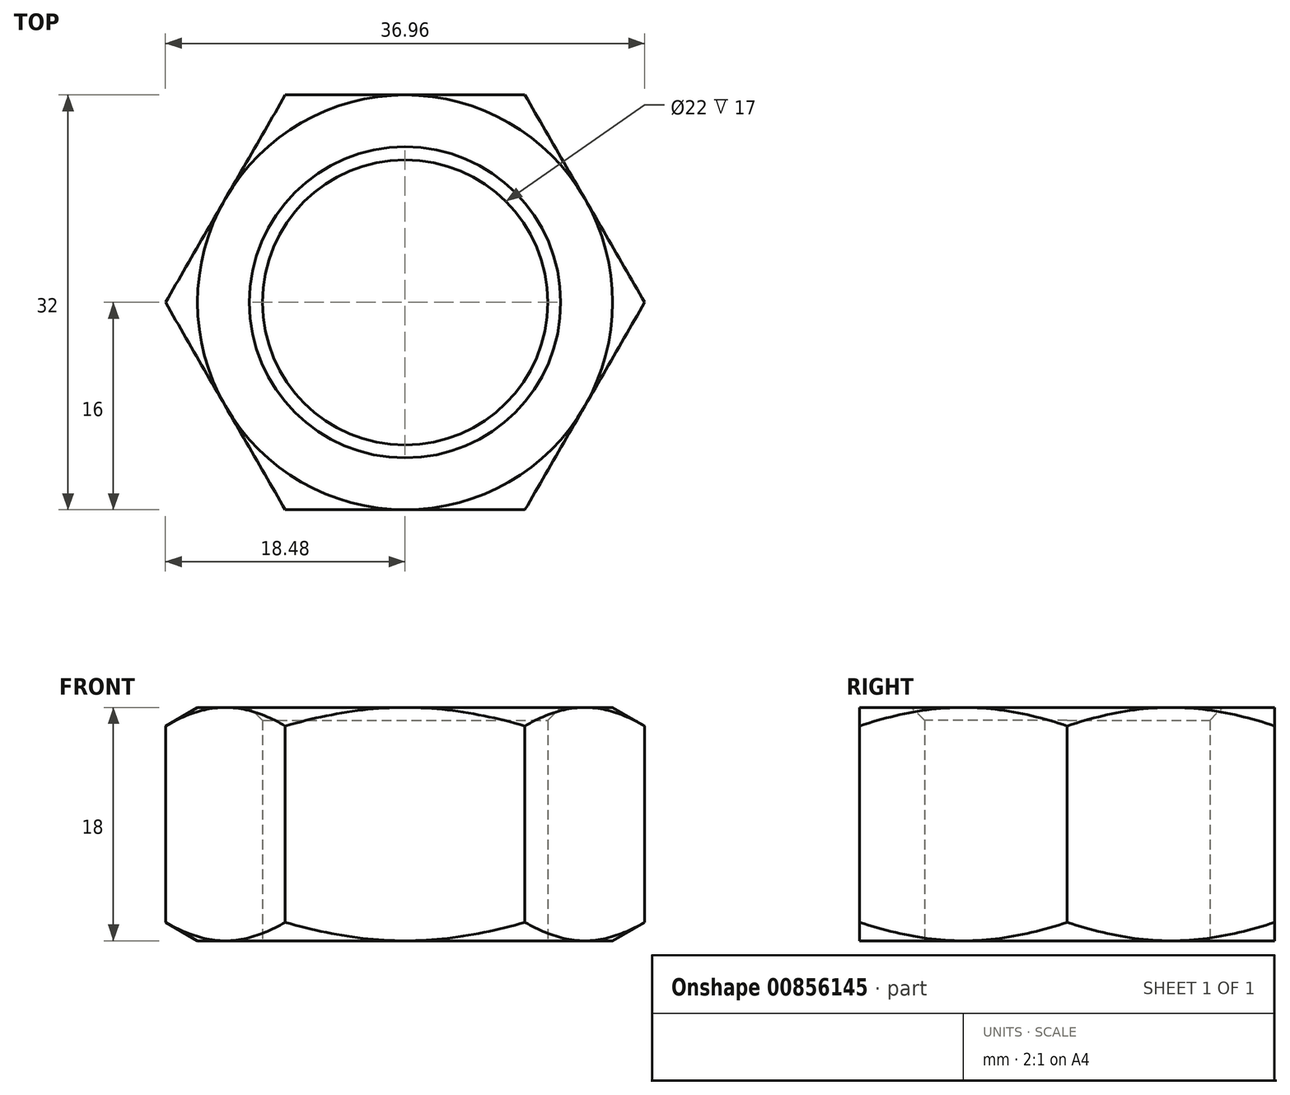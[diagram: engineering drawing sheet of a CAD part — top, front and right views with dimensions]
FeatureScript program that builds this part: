
annotation { "Feature Type Name" : "Feature", "Feature Type Description" : "" }
export const myFeature = defineFeature(function(context is Context, id is Id, definition is map)
    precondition{}
    {
        {
            var Q0;
            Q0=qCreatedBy(makeId("Top.planeOp"),FACE);
            var sketch = newSketch(context, id + "F0", { "sketchPlane" : qUnion([Q0])});
            skCircle(sketch, "E0.cCircle", {"center": v(0, 0) * mm, "radius": 16 * mm, "construction": true});
            skLineSegment(sketch, "E0.0", {"start": v(9.24, 16) * mm, "end": v(18.48, 0) * mm});
            skLineSegment(sketch, "E0.1", {"start": v(18.48, 0) * mm, "end": v(9.24, -16) * mm});
            skLineSegment(sketch, "E0.2", {"start": v(9.24, -16) * mm, "end": v(-9.24, -16) * mm});
            skLineSegment(sketch, "E0.3", {"start": v(-9.24, -16) * mm, "end": v(-18.48, 0) * mm});
            skLineSegment(sketch, "E0.4", {"start": v(-18.48, 0) * mm, "end": v(-9.24, 16) * mm});
            skLineSegment(sketch, "E0.5", {"start": v(-9.24, 16) * mm, "end": v(9.24, 16) * mm});
            skPoint(sketch, "E0.0.midPoint", {"position": v(13.86, 8) * mm});
            skSolve(sketch);
        }
        {
            var Q0;
            Q0=makeQuery(id+"F0.imprint","IMPRINT",FACE,{"disambiguationData":[TD([[makeQuery(id+"F0.imprint","IMPRINT",EDGE,{"derivedFrom":sQuery(id+"F0.wireOp",EDGE,"E0.0")}),-1.0]])]});
            extrude(context, id + "F1", {"entities" : qUnion([Q0]), "depth" : 18 * mm, "offsetDistance" : 25 * mm});
        }
        {
            var Q0;
            Q0=qCreatedBy(makeId("Right.planeOp"),FACE);
            var sketch = newSketch(context, id + "F2", { "sketchPlane" : qUnion([Q0])});
            skLineSegment(sketch, "E1", {"start": v(-16, 18) * mm, "end": v(-29.05, 18) * mm});
            skLineSegment(sketch, "E2", {"start": v(-29.05, 18) * mm, "end": v(-29.05, 10.47) * mm});
            skLineSegment(sketch, "E3", {"start": v(-29.05, 10.47) * mm, "end": v(-16, 18) * mm});
            skLineSegment(sketch, "E4", {"start": v(0, 0) * mm, "end": v(0, 20.15) * mm, "construction": true});
            skLineSegment(sketch, "E5", {"start": v(-16, 9) * mm, "end": v(24.29, 9) * mm, "construction": true});
            skLineSegment(sketch, "E6.MirrorCS", {"start": v(-29.05, 7.53) * mm, "end": v(-16, 0) * mm});
            skLineSegment(sketch, "E7.MirrorCS", {"start": v(-16, 0) * mm, "end": v(-29.05, 0) * mm});
            skLineSegment(sketch, "E8.MirrorCS", {"start": v(-29.05, 0) * mm, "end": v(-29.05, 7.53) * mm});
            skSolve(sketch);
        }
        {
            var Q0;
            Q0=makeQuery(id+"F2.imprint","IMPRINT",FACE,{"disambiguationData":[TD([[makeQuery(id+"F2.imprint","IMPRINT",EDGE,{"derivedFrom":sQuery(id+"F2.wireOp",EDGE,"E1")}),1.0]])]});
            var Q1;
            {var subQ5=sQuery(id+"F2.wireOp",EDGE,"E7.MirrorCS");Q1=makeQuery(id+"F2.imprint","IMPRINT",FACE,{"disambiguationData":[TD([[makeQuery(id+"F2.imprint","IMPRINT",EDGE,{"derivedFrom":subQ5}),-1.0]])]});}
            var Q2;
            {var subQ0=sQuery(id+"F2.wireOp",EDGE,"E8.MirrorCS");var subQ1=sQuery(id+"F2.wireOp",EDGE,"E3");var subQ2=makeQuery(id+"F2.imprint","INTERSECT",VERTEX,{"derivedFrom":[subQ1,subQ0]});Q2=makeQuery(id+"F2.imprint","IMPRINT",FACE,{"disambiguationData":[TD([[makeQuery(id+"F2.imprint","IMPRINT",EDGE,{"disambiguationData":[TD([[subQ2,-1.0]])],"derivedFrom":subQ1}),1.0]])]});}
            var Q3;
            Q3=sQuery(id+"F2.wireOp",EDGE,"E4");
            revolve(context, id + "F3", {"operationType" : NewBodyOperationType.REMOVE, "surfaceOperationType" : NewSurfaceOperationType.NEW, "entities" : qUnion([Q0, Q1, Q2]), "axis" : qUnion([Q3]), "revolveType" : RevolveType.FULL, "oppositeDirection" : true});
        }
        {
            var Q0;
            Q0=makeQuery(id+"F1.opExtrude","CAP_FACE",FACE,{"disambiguationData":[OSD([sQuery(id+"F0.wireOp",EDGE,"E0.0"),sQuery(id+"F0.wireOp",EDGE,"E0.1"),sQuery(id+"F0.wireOp",EDGE,"E0.2"),sQuery(id+"F0.wireOp",EDGE,"E0.3"),sQuery(id+"F0.wireOp",EDGE,"E0.4"),sQuery(id+"F0.wireOp",EDGE,"E0.5")])],"isStart":true});
            var sketch = newSketch(context, id + "F4", { "sketchPlane" : qUnion([Q0])});
            skCircle(sketch, "E9", {"center": v(0, 0) * mm, "radius": 11 * mm});
            skSolve(sketch);
        }
        {
            var Q0;
            Q0=makeQuery(id+"F4.imprint","IMPRINT",FACE,{"disambiguationData":[TD([[makeQuery(id+"F4.imprint","IMPRINT",EDGE,{"derivedFrom":sQuery(id+"F4.wireOp",EDGE,"E9")}),1.0]])]});
            extrude(context, id + "F5", {"entities" : qUnion([Q0]), "operationType" : NewBodyOperationType.REMOVE, "endBound" : BoundingType.THROUGH_ALL, "oppositeDirection" : true, "depth" : 25 * mm, "offsetDistance" : 25 * mm});
        }
        {
            var Q0;
            Q0=makeQuery(id+"F5.boolean.opBoolean","COPY",EDGE,{"derivedFrom":makeQuery(id+"F5.opExtrude","CAP_EDGE",EDGE,{"disambiguationData":[OSD([sQuery(id+"F4.wireOp",EDGE,"E9")])],"isStart":true})});
            var Q1;
            Q1=makeQuery(id+"F5.boolean.opBoolean","INTERSECT",EDGE,{"derivedFrom":[makeQuery(id+"F1.opExtrude","CAP_FACE",FACE,{"disambiguationData":[OSD([sQuery(id+"F0.wireOp",EDGE,"E0.0"),sQuery(id+"F0.wireOp",EDGE,"E0.1"),sQuery(id+"F0.wireOp",EDGE,"E0.2"),sQuery(id+"F0.wireOp",EDGE,"E0.3"),sQuery(id+"F0.wireOp",EDGE,"E0.4"),sQuery(id+"F0.wireOp",EDGE,"E0.5")])],"isStart":false}),makeQuery(id+"F5.opExtrude","SWEPT_FACE",FACE,{"disambiguationData":[OSD([sQuery(id+"F4.wireOp",EDGE,"E9")])]})]});
            chamfer(context, id + "F6", {"entities" : qUnion([Q0, Q1]), "width" : 1 * mm, "tangentPropagation" : true});
        }
    });
